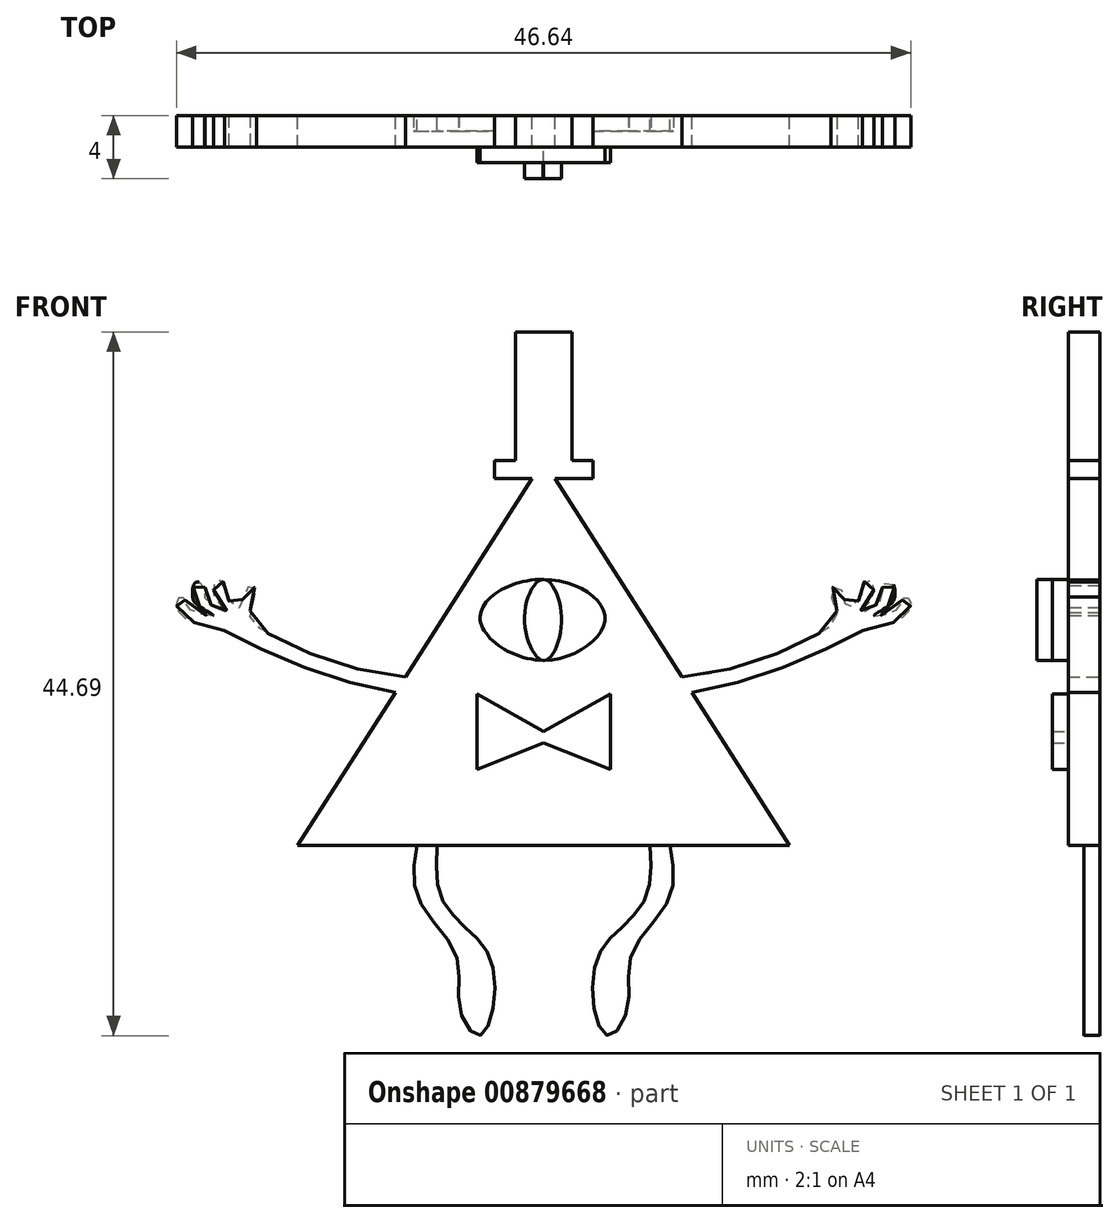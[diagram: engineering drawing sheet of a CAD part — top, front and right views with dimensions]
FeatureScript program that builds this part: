
annotation { "Feature Type Name" : "Feature", "Feature Type Description" : "" }
export const myFeature = defineFeature(function(context is Context, id is Id, definition is map)
    precondition{}
    {
        {
            var Q0;
            Q0=qCreatedBy(makeId("Front.planeOp"),FACE);
            var sketch = newSketch(context, id + "F0", { "sketchPlane" : qUnion([Q0])});
            skLineSegment(sketch, "E0", {"start": v(0, 46.86) * mm, "end": v(-15.62, 22.4) * mm});
            skLineSegment(sketch, "E1", {"start": v(-15.62, 22.4) * mm, "end": v(0, 22.4) * mm});
            skLineSegment(sketch, "E2.MirrorCS", {"start": v(0, 46.86) * mm, "end": v(15.62, 22.4) * mm});
            skLineSegment(sketch, "E3.MirrorCS", {"start": v(15.62, 22.4) * mm, "end": v(0, 22.4) * mm});
            skSolve(sketch);
        }
        {
            var Q0;
            Q0=makeQuery(id+"F0.imprint","IMPRINT",FACE,{"disambiguationData":[TD([[makeQuery(id+"F0.imprint","IMPRINT",EDGE,{"derivedFrom":sQuery(id+"F0.wireOp",EDGE,"E0")}),1.0]])]});
            extrude(context, id + "F1", {"entities" : qUnion([Q0]), "depth" : 2 * mm, "offsetDistance" : 25.4 * mm});
        }
        {
            var Q0;
            Q0=makeQuery(id+"F1.opExtrude","CAP_FACE",FACE,{"disambiguationData":[OSD([sQuery(id+"F0.wireOp",EDGE,"E0"),sQuery(id+"F0.wireOp",EDGE,"E1"),sQuery(id+"F0.wireOp",EDGE,"E2.MirrorCS"),sQuery(id+"F0.wireOp",EDGE,"E3.MirrorCS")])],"isStart":false});
            var sketch = newSketch(context, id + "F2", { "sketchPlane" : qUnion([Q0])});
            skFitSpline(sketch, "E4", {"points": [v(-4.03, 36.9) * mm, v(0, 39.3) * mm, v(3.9, 36.86) * mm, v(0, 34.16) * mm, v(-4.03, 36.9) * mm]});
            skSolve(sketch);
        }
        {
            var Q0;
            Q0=makeQuery(id+"F2.imprint","IMPRINT",FACE,{"disambiguationData":[TD([[makeQuery(id+"F2.imprint","IMPRINT",EDGE,{"derivedFrom":sQuery(id+"F2.wireOp",EDGE,"E4")}),-1.0]])]});
            extrude(context, id + "F3", {"entities" : qUnion([Q0]), "operationType" : NewBodyOperationType.ADD, "depth" : 1 * mm, "offsetDistance" : 25 * mm});
        }
        {
            var Q0;
            Q0=makeQuery(id+"F3.opExtrude","CAP_FACE",FACE,{"disambiguationData":[OSD([sQuery(id+"F2.wireOp",EDGE,"E4")])],"isStart":false});
            var sketch = newSketch(context, id + "F4", { "sketchPlane" : qUnion([Q0])});
            skFitSpline(sketch, "E5", {"points": [v(0, 39.3) * mm, v(-1.21, 36.88) * mm, v(0, 34.16) * mm, v(1.13, 36.68) * mm, v(0, 39.3) * mm]});
            skSolve(sketch);
        }
        {
            var Q0;
            {var subQ0=sQuery(id+"F4.wireOp",EDGE,"E5");var subQ1=makeQuery(id+"F3.opExtrude","CAP_EDGE",EDGE,{"disambiguationData":[OSD([sQuery(id+"F2.wireOp",EDGE,"E4")])],"isStart":false});var subQ2=makeQuery(id+"F4.imprint","INTERSECT",VERTEX,{"disambiguationData":[OD(0.0)],"derivedFrom":[subQ1,subQ0]});Q0=makeQuery(id+"F4.imprint","IMPRINT",FACE,{"disambiguationData":[TD([[makeQuery(id+"F4.imprint","IMPRINT",EDGE,{"disambiguationData":[TD([[subQ2,-1.0]])],"derivedFrom":subQ0}),1.0]])]});}
            extrude(context, id + "F5", {"entities" : qUnion([Q0]), "operationType" : NewBodyOperationType.ADD, "depth" : 1 * mm, "offsetDistance" : 25 * mm});
        }
        {
            var Q0;
            Q0=makeQuery(id+"F1.opExtrude","CAP_FACE",FACE,{"disambiguationData":[OSD([sQuery(id+"F0.wireOp",EDGE,"E0"),sQuery(id+"F0.wireOp",EDGE,"E1"),sQuery(id+"F0.wireOp",EDGE,"E2.MirrorCS"),sQuery(id+"F0.wireOp",EDGE,"E3.MirrorCS")])],"isStart":false});
            var sketch = newSketch(context, id + "F6", { "sketchPlane" : qUnion([Q0])});
            skLineSegment(sketch, "E6", {"start": v(0, 29.65) * mm, "end": v(-4.23, 32.03) * mm});
            skLineSegment(sketch, "E7", {"start": v(-4.23, 32.03) * mm, "end": v(-4.23, 27.22) * mm});
            skLineSegment(sketch, "E8", {"start": v(-4.23, 27.22) * mm, "end": v(0, 28.9) * mm});
            skLineSegment(sketch, "E9.MirrorCS", {"start": v(0, 29.65) * mm, "end": v(4.23, 32.03) * mm});
            skLineSegment(sketch, "E10.MirrorCS", {"start": v(4.23, 32.03) * mm, "end": v(4.23, 27.22) * mm});
            skLineSegment(sketch, "E11.MirrorCS", {"start": v(4.23, 27.22) * mm, "end": v(0, 28.9) * mm});
            skSolve(sketch);
        }
        {
            var Q0;
            Q0=makeQuery(id+"F6.imprint","IMPRINT",FACE,{"disambiguationData":[TD([[makeQuery(id+"F6.imprint","IMPRINT",EDGE,{"derivedFrom":sQuery(id+"F6.wireOp",EDGE,"E6")}),1.0]])]});
            extrude(context, id + "F7", {"entities" : qUnion([Q0]), "operationType" : NewBodyOperationType.ADD, "depth" : 1 * mm, "offsetDistance" : 25 * mm});
        }
        {
            var Q0;
            Q0=qCreatedBy(makeId("Front.planeOp"),FACE);
            var sketch = newSketch(context, id + "F8", { "sketchPlane" : qUnion([Q0])});
            skFitSpline(sketch, "E12", {"points": [v(-8.02, 22.48) * mm, v(-7.96, 19) * mm, v(-5.56, 15.46) * mm, v(-5.33, 12.04) * mm, v(-4.13, 10.32) * mm, v(-3.28, 11.7) * mm, v(-3.4, 15.23) * mm, v(-4.88, 17.12) * mm, v(-6.53, 19.17) * mm, v(-6.76, 22.42) * mm], "startDerivative": vector(-5.37, -29.46) * mm, "endDerivative": vector(1.78, 29.72) * mm});
            skLineSegment(sketch, "E13", {"start": v(-6.76, 22.42) * mm, "end": v(-8.02, 22.48) * mm});
            skSolve(sketch);
        }
        {
            var Q0;
            Q0=makeQuery(id+"F8.imprint","IMPRINT",FACE,{"disambiguationData":[TD([[makeQuery(id+"F8.imprint","IMPRINT",EDGE,{"derivedFrom":sQuery(id+"F8.wireOp",EDGE,"E12")}),1.0]])]});
            extrude(context, id + "F9", {"entities" : qUnion([Q0]), "depth" : 1 * mm, "offsetDistance" : 25 * mm});
        }
        {
            var Q0;
            Q0=makeQuery(id+"F9.opExtrude","SWEPT_BODY",BODY,{"disambiguationData":[OSD([sQuery(id+"F8.wireOp",EDGE,"E12"),sQuery(id+"F8.wireOp",EDGE,"E13")])]});
            var Q1;
            Q1=qCreatedBy(makeId("Right.planeOp"),FACE);
            mirror(context, id + "F10", {"operationType" : NewBodyOperationType.ADD, "entities" : qUnion([Q0]), "mirrorPlane" : qUnion([Q1])});
        }
        {
            var Q0;
            Q0=qCreatedBy(makeId("Front.planeOp"),FACE);
            var sketch = newSketch(context, id + "F11", { "sketchPlane" : qUnion([Q0])});
            skFitSpline(sketch, "E14", {"points": [v(-8.68, 33.1) * mm, v(-13.27, 34.01) * mm, v(-17.4, 35.81) * mm, v(-18.65, 37.11) * mm, v(-18.23, 38.52) * mm, v(-18.6, 38.89) * mm, v(-19.07, 38.2) * mm, v(-19.33, 37.48) * mm, v(-20.27, 38.42) * mm, v(-20.27, 39.05) * mm, v(-20.8, 39.26) * mm, v(-20.95, 38.79) * mm, v(-20.8, 37.95) * mm, v(-20, 37.16) * mm, v(-21.21, 37.74) * mm, v(-21.53, 38.42) * mm, v(-21.58, 38.94) * mm, v(-22.1, 39.1) * mm, v(-22.31, 38.42) * mm, v(-22, 37.69) * mm, v(-21, 37) * mm, v(-22.57, 37.48) * mm, v(-22.83, 38.1) * mm, v(-23.2, 38.1) * mm, v(-23.25, 37.43) * mm, v(-22.36, 36.64) * mm, v(-20.64, 36.17) * mm, v(-17.69, 34.75) * mm, v(-13.53, 33.14) * mm, v(-9.34, 32.1) * mm], "startDerivative": vector(-71.26, 6.62) * mm, "endDerivative": vector(66.83, -11.57) * mm});
            skLineSegment(sketch, "E15", {"start": v(-8.68, 33.1) * mm, "end": v(-9.34, 32.1) * mm});
            skSolve(sketch);
        }
        {
            var Q0;
            Q0=makeQuery(id+"F11.imprint","IMPRINT",FACE,{"disambiguationData":[TD([[makeQuery(id+"F11.imprint","IMPRINT",EDGE,{"derivedFrom":sQuery(id+"F11.wireOp",EDGE,"E14")}),1.0]])]});
            extrude(context, id + "F12", {"entities" : qUnion([Q0]), "depth" : 2 * mm, "offsetDistance" : 25 * mm});
        }
        {
            var Q0;
            Q0=makeQuery(id+"F12.opExtrude","SWEPT_BODY",BODY,{"disambiguationData":[OSD([sQuery(id+"F11.wireOp",EDGE,"E14"),sQuery(id+"F11.wireOp",EDGE,"E15")])]});
            var Q1;
            Q1=qCreatedBy(makeId("Right.planeOp"),FACE);
            mirror(context, id + "F13", {"operationType" : NewBodyOperationType.ADD, "entities" : qUnion([Q0]), "mirrorPlane" : qUnion([Q1])});
        }
        {
            var Q0;
            Q0=qCreatedBy(makeId("Front.planeOp"),FACE);
            var sketch = newSketch(context, id + "F14", { "sketchPlane" : qUnion([Q0])});
            skLineSegment(sketch, "E16", {"start": v(0, 45.71) * mm, "end": v(-3.12, 45.71) * mm});
            skLineSegment(sketch, "E17", {"start": v(-3.12, 45.71) * mm, "end": v(-3.12, 46.85) * mm});
            skLineSegment(sketch, "E18", {"start": v(-3.12, 46.85) * mm, "end": v(0, 46.85) * mm});
            skLineSegment(sketch, "E19.MirrorCS", {"start": v(3.12, 46.85) * mm, "end": v(0, 46.85) * mm});
            skLineSegment(sketch, "E20.MirrorCS", {"start": v(3.12, 45.71) * mm, "end": v(3.12, 46.85) * mm});
            skLineSegment(sketch, "E21.MirrorCS", {"start": v(0, 45.71) * mm, "end": v(3.12, 45.71) * mm});
            skLineSegment(sketch, "E22", {"start": v(-1.8, 46.85) * mm, "end": v(-1.8, 55) * mm});
            skLineSegment(sketch, "E23", {"start": v(-1.8, 55) * mm, "end": v(0, 55) * mm});
            skLineSegment(sketch, "E24.MirrorCS", {"start": v(1.8, 55) * mm, "end": v(0, 55) * mm});
            skLineSegment(sketch, "E25.MirrorCS", {"start": v(1.8, 46.85) * mm, "end": v(1.8, 55) * mm});
            skSolve(sketch);
        }
        {
            var Q0;
            Q0=makeQuery(id+"F14.imprint","IMPRINT",FACE,{"disambiguationData":[TD([[makeQuery(id+"F14.imprint","IMPRINT",EDGE,{"derivedFrom":sQuery(id+"F14.wireOp",EDGE,"E16")}),-1.0]])]});
            var Q1;
            {var subQ4=sQuery(id+"F14.wireOp",EDGE,"E22");Q1=makeQuery(id+"F14.imprint","IMPRINT",FACE,{"disambiguationData":[TD([[makeQuery(id+"F14.imprint","IMPRINT",EDGE,{"derivedFrom":subQ4}),-1.0]])]});}
            extrude(context, id + "F15", {"entities" : qUnion([Q0, Q1]), "operationType" : NewBodyOperationType.ADD, "depth" : 2 * mm, "offsetDistance" : 25 * mm});
        }
    });
